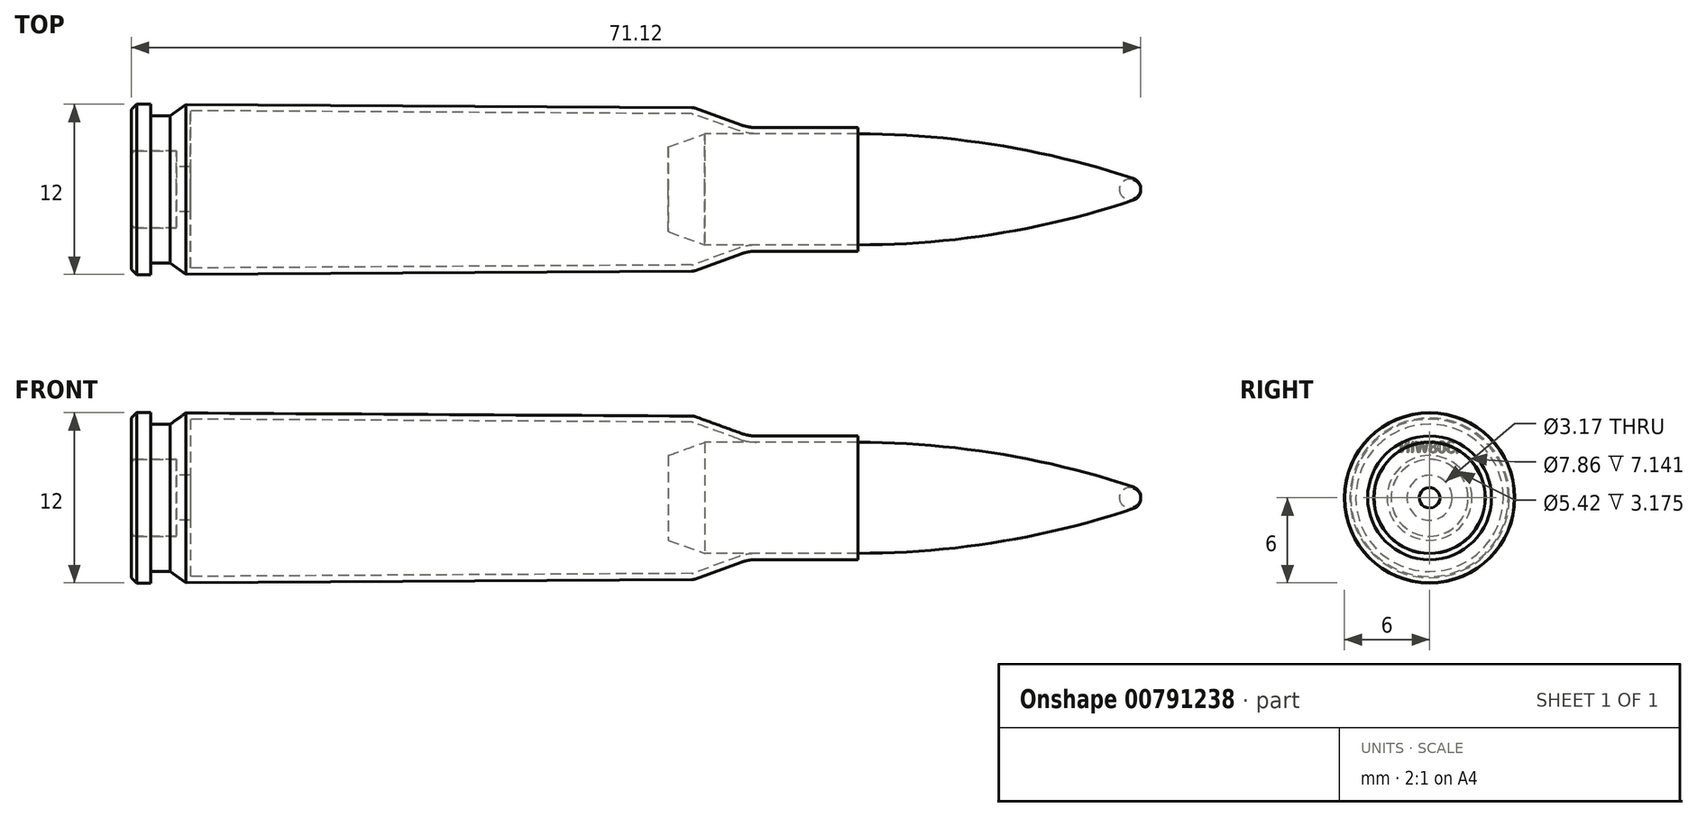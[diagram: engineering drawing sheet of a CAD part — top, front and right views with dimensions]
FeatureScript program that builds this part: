
annotation { "Feature Type Name" : "Feature", "Feature Type Description" : "" }
export const myFeature = defineFeature(function(context is Context, id is Id, definition is map)
    precondition{}
    {
        {
            var Q0;
            Q0=qCreatedBy(makeId("Front.planeOp"),FACE);
            var sketch = newSketch(context, id + "F0", { "sketchPlane" : qUnion([Q0])});
            skLineSegment(sketch, "E0", {"start": v(-35.56, 0) * mm, "end": v(35.56, 0) * mm});
            skPoint(sketch, "E1", {"position": v(0, 0) * mm});
            skLineSegment(sketch, "E2.top", {"start": v(-35.18, 6) * mm, "end": v(-34.2, 6) * mm});
            skLineSegment(sketch, "E2.left", {"start": v(-35.56, 0) * mm, "end": v(-35.56, 5.62) * mm});
            skLineSegment(sketch, "E3", {"start": v(4.18, 5.72) * mm, "end": v(7.4, 4.55) * mm});
            skLineSegment(sketch, "E4", {"start": v(8.48, 4.36) * mm, "end": v(15.62, 4.36) * mm});
            skLineSegment(sketch, "E5", {"start": v(15.62, 4.36) * mm, "end": v(15.62, 0) * mm});
            skArc(sketch, "E6", {"start": v(35.56, 0) * mm, "mid": v(35.43, 0.47) * mm, "end": v(35.04, 0.76) * mm});
            skLineSegment(sketch, "E7", {"start": v(4.83, 3.91) * mm, "end": v(15.62, 3.91) * mm});
            skArc(sketch, "E8", {"start": v(35.04, 0.76) * mm, "mid": v(25.46, 3.12) * mm, "end": v(15.62, 3.91) * mm});
            skLineSegment(sketch, "E9", {"start": v(2.29, 2.99) * mm, "end": v(2.29, 0) * mm});
            skLineSegment(sketch, "E10", {"start": v(-34.2, 6) * mm, "end": v(-34.2, 5.2) * mm});
            skLineSegment(sketch, "E11", {"start": v(-34.2, 5.2) * mm, "end": v(-32.8, 5.2) * mm});
            skLineSegment(sketch, "E12", {"start": v(-32.8, 5.2) * mm, "end": v(-31.7, 5.98) * mm});
            skLineSegment(sketch, "E13.trimOffspring", {"start": v(-31.7, 5.98) * mm, "end": v(3.93, 5.77) * mm});
            skPoint(sketch, "E14.visualSharp", {"position": v(4.06, 5.76) * mm});
            skArc(sketch, "E14.filletArc", {"start": v(4.18, 5.72) * mm, "mid": v(4.06, 5.75) * mm, "end": v(3.93, 5.77) * mm});
            skPoint(sketch, "E15.visualSharp", {"position": v(7.92, 4.36) * mm});
            skArc(sketch, "E15.filletArc", {"start": v(7.4, 4.55) * mm, "mid": v(7.93, 4.4) * mm, "end": v(8.48, 4.36) * mm});
            skLineSegment(sketch, "E16", {"start": v(-35.56, 5.62) * mm, "end": v(-35.18, 6) * mm});
            skLineSegment(sketch, "E17", {"start": v(2.29, 2.99) * mm, "end": v(4.83, 3.91) * mm});
            skSolve(sketch);
        }
        {
            var Q0;
            Q0=makeQuery(id+"F0.imprint","IMPRINT",FACE,{"disambiguationData":[TD([[makeQuery(id+"F0.imprint","IMPRINT",EDGE,{"derivedFrom":sQuery(id+"F0.wireOp",EDGE,"E2.top")}),-1.0]])]});
            var Q1;
            {var subQ3=sQuery(id+"F0.wireOp",EDGE,"E9");Q1=makeQuery(id+"F0.imprint","IMPRINT",FACE,{"disambiguationData":[TD([[makeQuery(id+"F0.imprint","IMPRINT",EDGE,{"derivedFrom":subQ3}),1.0]])]});}
            var Q2;
            Q2=sQuery(id+"F0.wireOp",EDGE,"E0");
            revolve(context, id + "F1", {"entities" : qUnion([Q0, Q1]), "axis" : qUnion([Q2]), "revolveType" : RevolveType.FULL, "surfaceOperationType" : NewSurfaceOperationType.NEW});
        }
        {
            var Q0;
            {var subQ4=sQuery(id+"F0.wireOp",EDGE,"E6");Q0=makeQuery(id+"F0.imprint","IMPRINT",FACE,{"disambiguationData":[TD([[makeQuery(id+"F0.imprint","IMPRINT",EDGE,{"derivedFrom":subQ4}),1.0]])]});}
            var Q1;
            {var subQ3=sQuery(id+"F0.wireOp",EDGE,"E9");Q1=makeQuery(id+"F0.imprint","IMPRINT",FACE,{"disambiguationData":[TD([[makeQuery(id+"F0.imprint","IMPRINT",EDGE,{"derivedFrom":subQ3}),1.0]])]});}
            var Q2;
            Q2=sQuery(id+"F0.wireOp",EDGE,"E0");
            revolve(context, id + "F2", {"entities" : qUnion([Q0, Q1]), "axis" : qUnion([Q2]), "revolveType" : RevolveType.FULL});
        }
        {
            var Q0;
            Q0=makeQuery(id+"F1.opRevolve","SWEPT_FACE",FACE,{"disambiguationData":[OSD([sQuery(id+"F0.wireOp",EDGE,"E5")])]});
            shell(context, id + "F3", {"entities" : qUnion([Q0]), "thickness" : 0.43 * mm});
        }
        {
            var Q0;
            Q0=qCreatedBy(makeId("Front.planeOp"),FACE);
            var sketch = newSketch(context, id + "F4", { "sketchPlane" : qUnion([Q0])});
            skLineSegment(sketch, "E18.0", {"start": v(-35.56, 0) * mm, "end": v(-35.56, 5.62) * mm});
            skLineSegment(sketch, "E18.1", {"start": v(-35.56, 5.62) * mm, "end": v(-35.18, 6) * mm});
            skLineSegment(sketch, "E18.2", {"start": v(-35.18, 6) * mm, "end": v(-34.2, 6) * mm});
            skLineSegment(sketch, "E18.3", {"start": v(-34.2, 6) * mm, "end": v(-34.2, 5.2) * mm});
            skLineSegment(sketch, "E18.4", {"start": v(-34.2, 5.2) * mm, "end": v(-32.8, 5.2) * mm});
            skLineSegment(sketch, "E18.5", {"start": v(-32.8, 5.2) * mm, "end": v(-31.7, 5.98) * mm});
            skLineSegment(sketch, "E19", {"start": v(-31.7, 5.98) * mm, "end": v(-31.4, 5.98) * mm});
            skLineSegment(sketch, "E20", {"start": v(-35.56, 0) * mm, "end": v(-31.4, 0) * mm});
            skLineSegment(sketch, "E21", {"start": v(-31.4, 0) * mm, "end": v(-31.4, 5.98) * mm});
            skSolve(sketch);
        }
        {
            var Q0;
            Q0=qSketchRegion(id+"F4",true);
            var Q1;
            Q1=sQuery(id+"F4.wireOp",EDGE,"E20");
            revolve(context, id + "F5", {"operationType" : NewBodyOperationType.ADD, "entities" : qUnion([Q0]), "axis" : qUnion([Q1]), "revolveType" : RevolveType.FULL});
        }
        {
            var Q0;
            Q0=makeQuery(id+"F1.opRevolve","SWEPT_FACE",FACE,{"disambiguationData":[OSD([sQuery(id+"F0.wireOp",EDGE,"E2.left")])]});
            var sketch = newSketch(context, id + "F6", { "sketchPlane" : qUnion([Q0])});
            skCircle(sketch, "E22", {"center": v(0, 0) * mm, "radius": 2.71 * mm});
            skCircle(sketch, "E23", {"center": v(0, 0) * mm, "radius": 1.59 * mm});
            skSolve(sketch);
        }
        {
            var Q0;
            Q0=makeQuery(id+"F6.imprint","IMPRINT",FACE,{"disambiguationData":[TD([[makeQuery(id+"F6.imprint","IMPRINT",EDGE,{"derivedFrom":sQuery(id+"F6.wireOp",EDGE,"E23")}),1.0]])]});
            extrude(context, id + "F7", {"entities" : qUnion([Q0]), "operationType" : NewBodyOperationType.REMOVE, "endBound" : BoundingType.UP_TO_NEXT, "oppositeDirection" : true, "depth" : 25.4 * mm});
        }
        {
            var Q0;
            Q0=makeQuery(id+"F6.imprint","IMPRINT",FACE,{"disambiguationData":[TD([[makeQuery(id+"F6.imprint","IMPRINT",EDGE,{"derivedFrom":sQuery(id+"F6.wireOp",EDGE,"E22")}),1.0]])]});
            var Q1;
            Q1=makeQuery(id+"F1.opRevolve","SWEPT_FACE",FACE,{"disambiguationData":[OSD([sQuery(id+"F0.wireOp",EDGE,"E10")])]});
            extrude(context, id + "F8", {"entities" : qUnion([Q0]), "operationType" : NewBodyOperationType.REMOVE, "oppositeDirection" : true, "endBoundEntityFace" : qUnion([Q1]), "depth" : 3.17 * mm});
        }
        {
            var Q0;
            Q0=qCreatedBy(makeId("Front.planeOp"),FACE);
            var sketch = newSketch(context, id + "F9", { "sketchPlane" : qUnion([Q0])});
            skLineSegment(sketch, "E24", {"start": v(-32.39, 0) * mm, "end": v(-35.56, 0) * mm});
            skLineSegment(sketch, "E25", {"start": v(-35.56, 0) * mm, "end": v(-35.56, 2.32) * mm});
            skLineSegment(sketch, "E26", {"start": v(-35.18, 2.7) * mm, "end": v(-32.39, 2.7) * mm});
            skLineSegment(sketch, "E27", {"start": v(-32.39, 2.7) * mm, "end": v(-32.39, 0) * mm});
            skPoint(sketch, "E28.visualSharp", {"position": v(-35.56, 2.7) * mm});
            skArc(sketch, "E28.filletArc", {"start": v(-35.18, 2.7) * mm, "mid": v(-35.45, 2.6) * mm, "end": v(-35.56, 2.32) * mm});
            skSolve(sketch);
        }
        {
            var Q0;
            Q0=qSketchRegion(id+"F9",true);
            var Q1;
            Q1=sQuery(id+"F9.wireOp",EDGE,"E24");
            revolve(context, id + "F10", {"entities" : qUnion([Q0]), "axis" : qUnion([Q1]), "revolveType" : RevolveType.FULL});
        }
        {
            var Q0;
            Q0=makeQuery(id+"F1.opRevolve","SWEPT_FACE",FACE,{"disambiguationData":[OSD([sQuery(id+"F0.wireOp",EDGE,"E2.left")])]});
            var sketch = newSketch(context, id + "F11", { "sketchPlane" : qUnion([Q0])});
            skText(sketch, "E29", { "text": ".308WIN", "fontName": "NotoSansCJKjp-Regular.otf"});
            const initialGuessF11  = {"E29": [-0.0021, 0.00318, 1, 0, 0.0008]};
            skSetInitialGuess(sketch, initialGuessF11);
            skSolve(sketch);
        }
        {
            var Q0;
            Q0=qSketchRegion(id+"F11",true);
            extrude(context, id + "F12", {"entities" : qUnion([Q0]), "operationType" : NewBodyOperationType.REMOVE, "oppositeDirection" : true, "depth" : 0.03 * mm});
        }
    });
